# Revit family: Faucet-Bidet-KOHLER-AVID-K-97014BR_1
name_source: partatom
category: Plumbing Fixtures
revit_build: Autodesk Revit 2017 (Build: 20160225_1515(x64)
units: mm (PartAtom-declared; Revit-internal decimal feet)

## family parameters
Cut with Voids When Loaded = No
Host = Face
OmniClass Number = 23.31.11.00
OmniClass Title = Faucets
Part Type = Normal
Room Calculation Point = No
Round Connector Dimension = Use Diameter
Shared = No

## types (2) — shared parameters
ADA Compliant = No
Assembly Code = D2010
CW Connection = Yes
Cold Water Inlet = Cold Water Inlet
Date Modified = 06/21/2021
Default Elevation = 36"
Description = SC Bidet Mixer With Drain
Drain Included = Yes
Finish = Kohler-Metal-CP-Polished_Chrome
Flow Rate = 0 GPM
HW Connection = Yes
Handle Clearance = 4 1/4"
Height = 5 1/8"
Hot Water Inlet = Hot Water Inlet
Length = 4 3/4"
Manufacturer = KOHLER Co.
Master Format 2014 = 22 41 39
Master Format 2014 Name = Residential Faucets, Supplies, and Trim
Material = Brass Construction
Pressure = 0.00 psi
Product Name = AVID
Spout Reach = 4 3/4"
URL = https://br.kohler.com
Vent Connection = No
Waste Connection = No
Waste Water Outlet = Waste Water Outlet
WaterSense Certified = No
Width = 2"

## per-type parameters (varying)
| type | Model | Product Page URL | Type |
| CP-Polished Chrome | K-97014BR-CP |  | 1 |
| Lever Handle, CP-Polished Chrome | K-97014BR-4-CP | https://br.kohler.com | 2 |

## geometry (parser evidence)
native form markers: Sweep x5
no freeform markers — native parametric forms only
